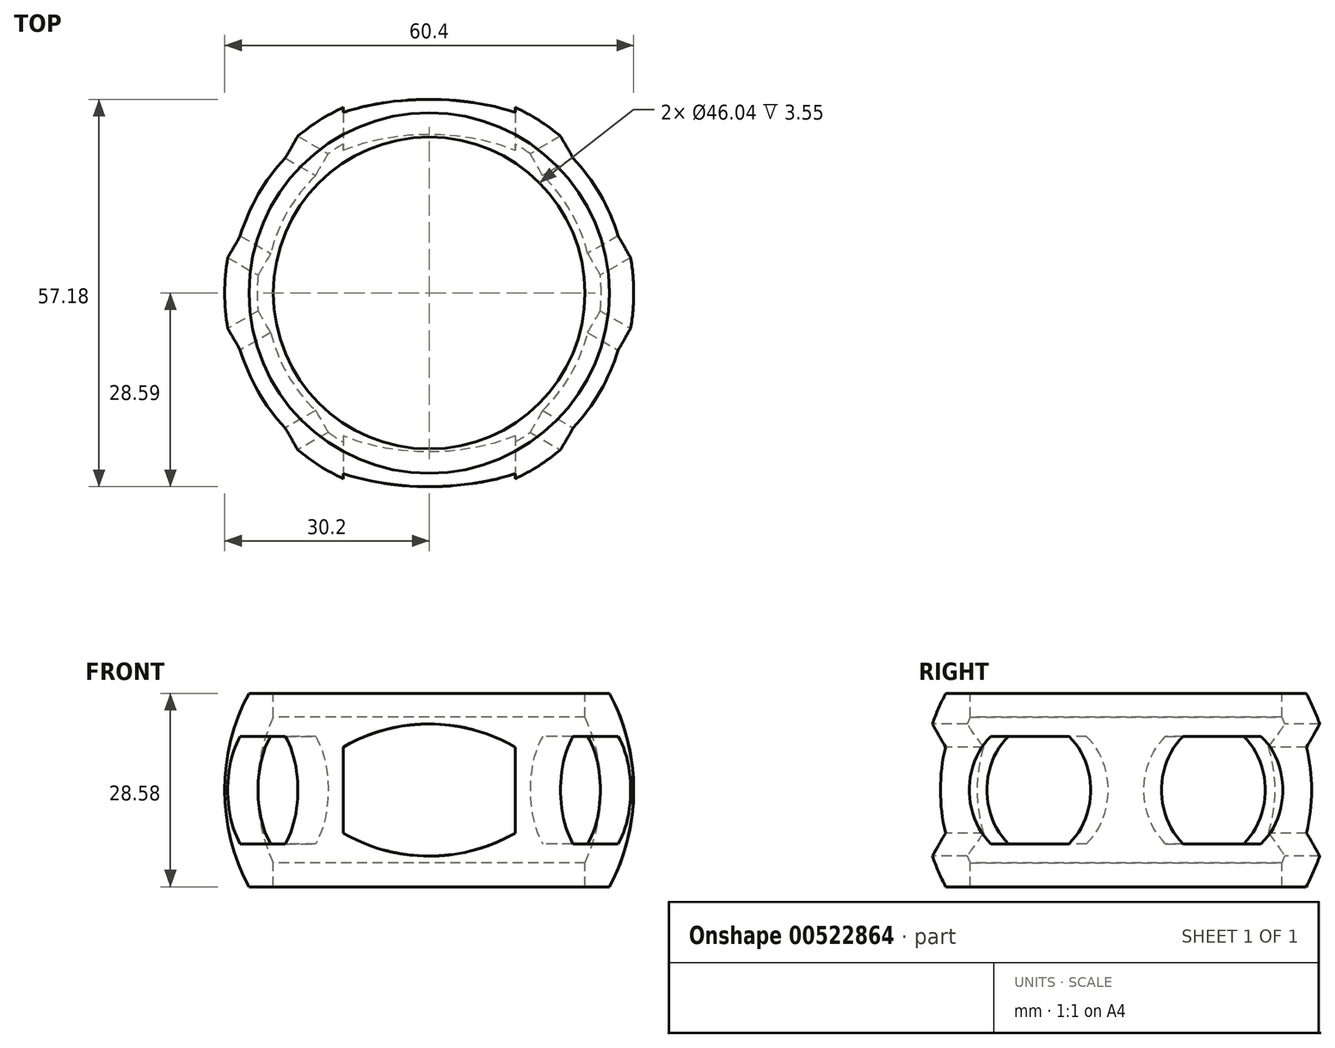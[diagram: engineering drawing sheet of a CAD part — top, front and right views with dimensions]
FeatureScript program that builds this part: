
annotation { "Feature Type Name" : "Feature", "Feature Type Description" : "" }
export const myFeature = defineFeature(function(context is Context, id is Id, definition is map)
    precondition{}
    {
        {
            var Q0;
            Q0=qCreatedBy(makeId("Front.planeOp"),FACE);
            var sketch = newSketch(context, id + "F0", { "sketchPlane" : qUnion([Q0])});
            skArc(sketch, "E0", {"start": v(23.02, -10.74) * mm, "mid": v(25.4, 0) * mm, "end": v(23.02, 10.74) * mm});
            skArc(sketch, "E1", {"start": v(26.61, -14.29) * mm, "mid": v(30.2, 0) * mm, "end": v(26.61, 14.29) * mm});
            skLineSegment(sketch, "E2.bottom", {"start": v(-26.61, 14.29) * mm, "end": v(-23.02, 14.29) * mm});
            skLineSegment(sketch, "E2.top", {"start": v(-26.61, -14.29) * mm, "end": v(-23.02, -14.29) * mm});
            skPoint(sketch, "E3.MirrorP", {"position": v(0, 28.58) * mm});
            skLineSegment(sketch, "E4", {"start": v(23.02, 14.29) * mm, "end": v(23.02, 10.74) * mm});
            skLineSegment(sketch, "E5", {"start": v(-23.02, 14.29) * mm, "end": v(-23.02, 10.74) * mm});
            skLineSegment(sketch, "E6", {"start": v(23.02, -10.74) * mm, "end": v(23.02, -14.29) * mm});
            skLineSegment(sketch, "E7", {"start": v(-23.02, -10.74) * mm, "end": v(-23.02, -14.29) * mm});
            skPoint(sketch, "E2.left.end.orphan", {"position": v(-41.98, -14.29) * mm});
            skPoint(sketch, "E8.orphan", {"position": v(-41.98, 14.29) * mm});
            skPoint(sketch, "E2.right.start.orphan", {"position": v(41.98, 14.29) * mm});
            skPoint(sketch, "E9.orphan", {"position": v(41.98, -14.29) * mm});
            skArc(sketch, "E10.trimOffspring", {"start": v(-23.02, 10.74) * mm, "mid": v(-25.4, 0) * mm, "end": v(-23.02, -10.74) * mm});
            skArc(sketch, "E11.trimOffspring", {"start": v(-26.61, 14.29) * mm, "mid": v(-30.2, 0) * mm, "end": v(-26.61, -14.29) * mm});
            skLineSegment(sketch, "E12.trimOffspring", {"start": v(23.02, -14.29) * mm, "end": v(26.61, -14.29) * mm});
            skPoint(sketch, "E13.orphan", {"position": v(0, 14.29) * mm});
            skLineSegment(sketch, "E14.trimOffspring", {"start": v(23.02, 14.29) * mm, "end": v(26.61, 14.29) * mm});
            skLineSegment(sketch, "E15", {"start": v(0, 28.58) * mm, "end": v(0, -37.66) * mm});
            skSolve(sketch);
        }
        {
            var Q0;
            Q0=makeQuery(id+"F0.imprint","IMPRINT",FACE,{"disambiguationData":[TD([[makeQuery(id+"F0.imprint","IMPRINT",EDGE,{"derivedFrom":sQuery(id+"F0.wireOp",EDGE,"E0")}),-1.0]])]});
            var Q1;
            Q1=sQuery(id+"F0.wireOp",EDGE,"E15");
            revolve(context, id + "F1", {"entities" : qUnion([Q0]), "axis" : qUnion([Q1]), "revolveType" : RevolveType.FULL});
        }
        {
            var Q0;
            Q0=qCreatedBy(makeId("Front.planeOp"),FACE);
            cPlane(context, id + "F2", {"entities" : qUnion([Q0]), "cplaneType" : CPlaneType.OFFSET, "offset" : 30.2 * mm, "width" : 152.4 * mm, "height" : 152.4 * mm});
        }
        {
            var Q0;
            Q0=qCreatedBy(id+"F2.planeOp",FACE);
            var sketch = newSketch(context, id + "F3", { "sketchPlane" : qUnion([Q0])});
            skLineSegment(sketch, "E16.bottom", {"start": v(-12.7, 6.35) * mm, "end": v(12.7, 6.35) * mm});
            skLineSegment(sketch, "E16.top", {"start": v(-12.7, -6.35) * mm, "end": v(12.7, -6.35) * mm});
            skLineSegment(sketch, "E16.left", {"start": v(-12.7, 6.35) * mm, "end": v(-12.7, -6.35) * mm});
            skLineSegment(sketch, "E16.right", {"start": v(12.7, 6.35) * mm, "end": v(12.7, -6.35) * mm});
            skPoint(sketch, "E16.middle", {"position": v(0, 0) * mm});
            skArc(sketch, "E17", {"start": v(12.7, 6.35) * mm, "mid": v(0, 9.75) * mm, "end": v(-12.7, 6.35) * mm});
            skArc(sketch, "E18", {"start": v(-12.7, -6.35) * mm, "mid": v(0, -9.75) * mm, "end": v(12.7, -6.35) * mm});
            skSolve(sketch);
        }
        {
            var Q0;
            Q0 = qSketchRegion(id + "F3", true);
            extrude(context, id + "F4", {"entities" : qUnion([Q0]), "operationType" : NewBodyOperationType.REMOVE, "oppositeDirection" : true, "depth" : 72.39 * mm, "offsetDistance" : 25.4 * mm});
        }
        {
            var Q0;
            Q0=sQuery(id+"F0.wireOp",EDGE,"E15");
            cPlane(context, id + "F5", {"entities" : qUnion([Q0]), "cplaneType" : CPlaneType.LINE_ANGLE, "offset" : 25.4 * mm, "angle" : 30 * degree, "oppositeDirection" : true, "width" : 152.4 * mm, "height" : 152.4 * mm});
        }
        {
            var Q0;
            Q0=qCreatedBy(id+"F5.planeOp",FACE);
            var sketch = newSketch(context, id + "F6", { "sketchPlane" : qUnion([Q0])});
            skLineSegment(sketch, "E19.bottom", {"start": v(6.64, 7.94) * mm, "end": v(-6.64, 7.94) * mm});
            skLineSegment(sketch, "E19.top", {"start": v(6.64, -7.94) * mm, "end": v(-6.64, -7.94) * mm});
            skPoint(sketch, "E19.middle", {"position": v(0, 0) * mm});
            skArc(sketch, "E20", {"start": v(-6.64, 7.94) * mm, "mid": v(-10.35, 0) * mm, "end": v(-6.64, -7.94) * mm});
            skArc(sketch, "E21.trimOffspring", {"start": v(6.64, -7.94) * mm, "mid": v(10.35, 0) * mm, "end": v(6.64, 7.94) * mm});
            skSolve(sketch);
        }
        {
            var Q0;
            Q0 = qSketchRegion(id + "F6", true);
            extrude(context, id + "F7", {"entities" : qUnion([Q0]), "operationType" : NewBodyOperationType.REMOVE, "endBound" : BoundingType.SYMMETRIC, "oppositeDirection" : true, "depth" : 106.17 * mm, "offsetDistance" : 25.4 * mm});
        }
        {
            var Q0;
            Q0=sQuery(id+"F0.wireOp",EDGE,"E15");
            cPlane(context, id + "F8", {"entities" : qUnion([Q0]), "cplaneType" : CPlaneType.LINE_ANGLE, "offset" : 25.4 * mm, "angle" : 30 * degree, "width" : 152.4 * mm, "height" : 152.4 * mm});
        }
        {
            var Q0;
            Q0=qCreatedBy(id+"F8.planeOp",FACE);
            var sketch = newSketch(context, id + "F9", { "sketchPlane" : qUnion([Q0])});
            skPoint(sketch, "E22.middle", {"position": v(0, 0) * mm});
            skLineSegment(sketch, "E23.bottom", {"start": v(6.64, 7.94) * mm, "end": v(-6.64, 7.94) * mm});
            skLineSegment(sketch, "E23.top", {"start": v(6.64, -7.94) * mm, "end": v(-6.64, -7.94) * mm});
            skArc(sketch, "E24", {"start": v(-6.64, 7.94) * mm, "mid": v(-10.35, 0) * mm, "end": v(-6.64, -7.94) * mm});
            skArc(sketch, "E25.trimOffspring", {"start": v(6.64, -7.94) * mm, "mid": v(10.35, 0) * mm, "end": v(6.64, 7.94) * mm});
            skSolve(sketch);
        }
        {
            var Q0;
            Q0=makeQuery(id+"F9.imprint","IMPRINT",FACE,{"disambiguationData":[TD([[makeQuery(id+"F9.imprint","IMPRINT",EDGE,{"derivedFrom":sQuery(id+"F9.wireOp",EDGE,"E22.bottom")}),-1.0]])]});
            var Q1;
            Q1=makeQuery(id+"F9.imprint","IMPRINT",FACE,{"disambiguationData":[TD([[makeQuery(id+"F9.imprint","IMPRINT",EDGE,{"derivedFrom":sQuery(id+"F9.wireOp",EDGE,"E22.bottom")}),1.0]])]});
            var Q2;
            Q2=makeQuery(id+"F9.imprint","IMPRINT",FACE,{"disambiguationData":[TD([[makeQuery(id+"F9.imprint","IMPRINT",EDGE,{"derivedFrom":sQuery(id+"F9.wireOp",EDGE,"E22.top")}),-1.0]])]});
            var Q3;
            Q3=makeQuery(id+"F9.imprint","IMPRINT",FACE,{"disambiguationData":[TD([[makeQuery(id+"F9.imprint","IMPRINT",EDGE,{"derivedFrom":sQuery(id+"F9.wireOp",EDGE,"E23.bottom")}),1.0]])]});
            extrude(context, id + "F10", {"entities" : qUnion([Q0, Q1, Q2, Q3]), "operationType" : NewBodyOperationType.REMOVE, "endBound" : BoundingType.SYMMETRIC, "depth" : 94.49 * mm, "offsetDistance" : 25.4 * mm});
        }
    });
